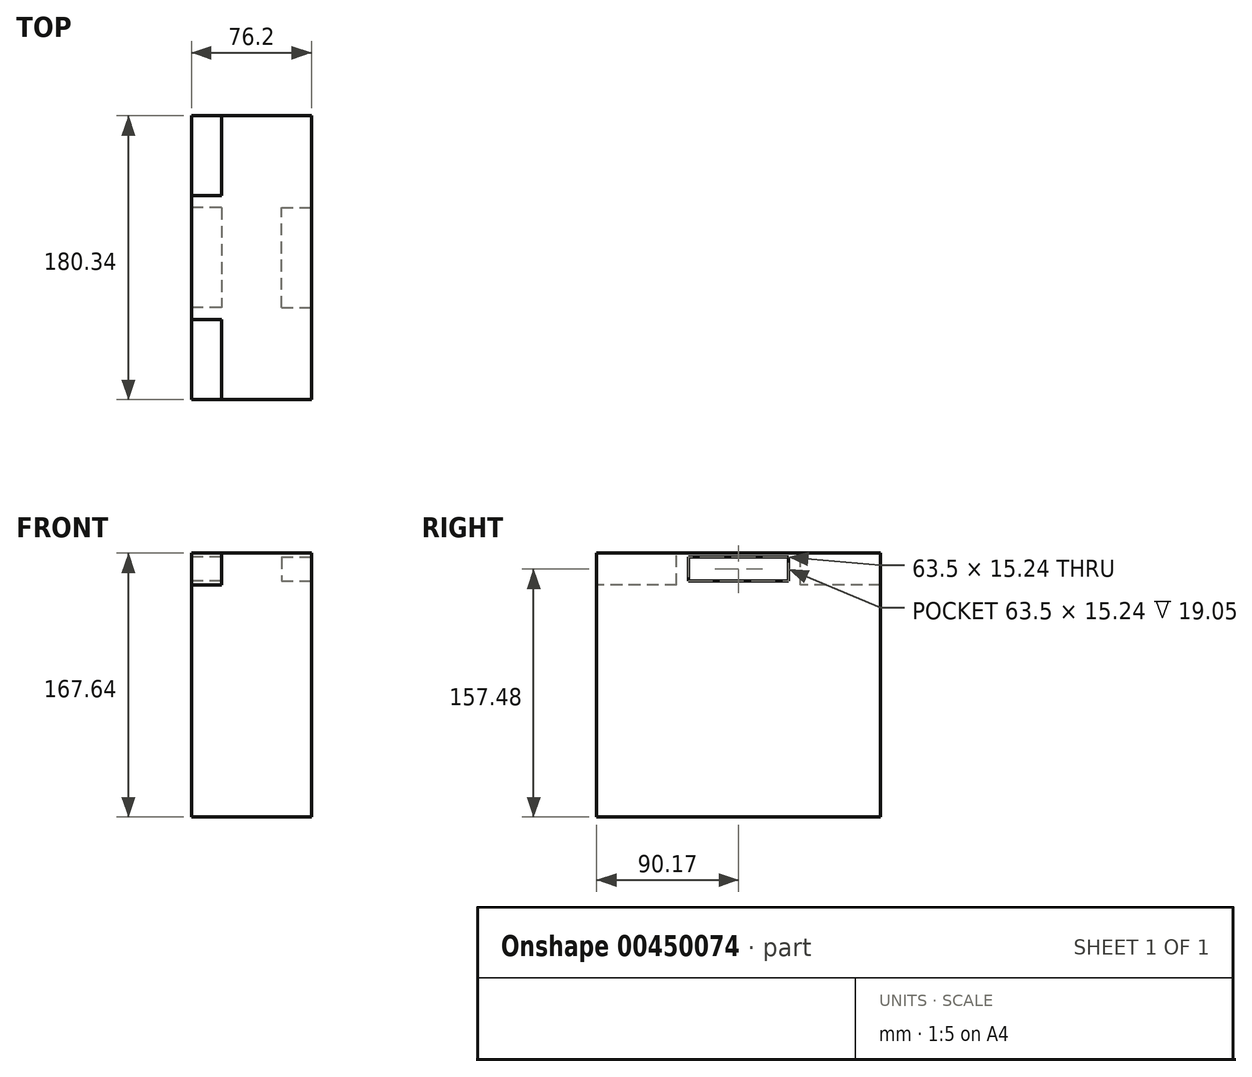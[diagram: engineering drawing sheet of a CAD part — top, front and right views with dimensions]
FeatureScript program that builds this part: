
annotation { "Feature Type Name" : "Feature", "Feature Type Description" : "" }
export const myFeature = defineFeature(function(context is Context, id is Id, definition is map)
    precondition{}
    {
        {
            var Q0;
            Q0=qCreatedBy(makeId("Top.planeOp"),FACE);
            var sketch = newSketch(context, id + "F0", { "sketchPlane" : qUnion([Q0])});
            skLineSegment(sketch, "E0.bottom", {"start": v(-38.1, 90.17) * mm, "end": v(38.1, 90.17) * mm});
            skLineSegment(sketch, "E0.top", {"start": v(-38.1, -90.17) * mm, "end": v(38.1, -90.17) * mm});
            skLineSegment(sketch, "E0.left", {"start": v(-38.1, 90.17) * mm, "end": v(-38.1, -90.17) * mm});
            skLineSegment(sketch, "E0.right", {"start": v(38.1, 90.17) * mm, "end": v(38.1, -90.17) * mm});
            skPoint(sketch, "E0.middle", {"position": v(0, 0) * mm});
            skSolve(sketch);
        }
        {
            var Q0;
            Q0=makeQuery(id+"F0.imprint","IMPRINT",FACE,{"disambiguationData":[TD([[makeQuery(id+"F0.imprint","IMPRINT",EDGE,{"derivedFrom":sQuery(id+"F0.wireOp",EDGE,"E0.bottom")}),-1.0]])]});
            extrude(context, id + "F1", {"entities" : qUnion([Q0]), "depth" : 167.64 * mm});
        }
        {
            var Q0;
            Q0=makeQuery(id+"F1.opExtrude","CAP_FACE",FACE,{"disambiguationData":[OSD([sQuery(id+"F0.wireOp",EDGE,"E0.bottom"),sQuery(id+"F0.wireOp",EDGE,"E0.top"),sQuery(id+"F0.wireOp",EDGE,"E0.left"),sQuery(id+"F0.wireOp",EDGE,"E0.right")])],"isStart":false});
            var sketch = newSketch(context, id + "F2", { "sketchPlane" : qUnion([Q0])});
            skLineSegment(sketch, "E1.bottom", {"start": v(-38.1, -90.17) * mm, "end": v(-19.05, -90.17) * mm});
            skLineSegment(sketch, "E1.top", {"start": v(-38.1, -39.37) * mm, "end": v(-19.05, -39.37) * mm});
            skLineSegment(sketch, "E1.left", {"start": v(-38.1, -90.17) * mm, "end": v(-38.1, -39.37) * mm});
            skLineSegment(sketch, "E1.right", {"start": v(-19.05, -90.17) * mm, "end": v(-19.05, -39.37) * mm});
            skLineSegment(sketch, "E2.bottom", {"start": v(-38.1, 90.17) * mm, "end": v(-19.05, 90.17) * mm});
            skLineSegment(sketch, "E2.top", {"start": v(-38.1, 39.37) * mm, "end": v(-19.05, 39.37) * mm});
            skLineSegment(sketch, "E2.left", {"start": v(-38.1, 90.17) * mm, "end": v(-38.1, 39.37) * mm});
            skLineSegment(sketch, "E2.right", {"start": v(-19.05, 90.17) * mm, "end": v(-19.05, 39.37) * mm});
            skSolve(sketch);
        }
        {
            var Q0;
            Q0=makeQuery(id+"F2.imprint","IMPRINT",FACE,{"disambiguationData":[TD([[makeQuery(id+"F2.imprint","IMPRINT",EDGE,{"derivedFrom":sQuery(id+"F2.wireOp",EDGE,"E1.bottom")}),1.0]])]});
            var Q1;
            Q1=makeQuery(id+"F2.imprint","IMPRINT",FACE,{"disambiguationData":[TD([[makeQuery(id+"F2.imprint","IMPRINT",EDGE,{"derivedFrom":sQuery(id+"F2.wireOp",EDGE,"E2.bottom")}),-1.0]])]});
            extrude(context, id + "F3", {"entities" : qUnion([Q0, Q1]), "operationType" : NewBodyOperationType.REMOVE, "oppositeDirection" : true, "depth" : 20.32 * mm});
        }
        {
            var Q0;
            Q0=makeQuery(id+"F1.opExtrude","SWEPT_FACE",FACE,{"disambiguationData":[OSD([sQuery(id+"F0.wireOp",EDGE,"E0.left")])]});
            var sketch = newSketch(context, id + "F4", { "sketchPlane" : qUnion([Q0])});
            skLineSegment(sketch, "E3.bottom", {"start": v(-31.75, 165.1) * mm, "end": v(31.75, 165.1) * mm});
            skLineSegment(sketch, "E3.top", {"start": v(-31.75, 149.86) * mm, "end": v(31.75, 149.86) * mm});
            skLineSegment(sketch, "E3.left", {"start": v(-31.75, 165.1) * mm, "end": v(-31.75, 149.86) * mm});
            skLineSegment(sketch, "E3.right", {"start": v(31.75, 165.1) * mm, "end": v(31.75, 149.86) * mm});
            skPoint(sketch, "E3.middle", {"position": v(0, 157.48) * mm});
            skSolve(sketch);
        }
        {
            var Q0;
            Q0=makeQuery(id+"F4.imprint","IMPRINT",FACE,{"disambiguationData":[TD([[makeQuery(id+"F4.imprint","IMPRINT",EDGE,{"derivedFrom":sQuery(id+"F4.wireOp",EDGE,"E3.bottom")}),-1.0]])]});
            extrude(context, id + "F5", {"entities" : qUnion([Q0]), "operationType" : NewBodyOperationType.REMOVE, "oppositeDirection" : true, "depth" : 19.05 * mm});
        }
        {
            var Q0;
            Q0=makeQuery(id+"F1.opExtrude","SWEPT_FACE",FACE,{"disambiguationData":[OSD([sQuery(id+"F0.wireOp",EDGE,"E0.right")])]});
            var sketch = newSketch(context, id + "F6", { "sketchPlane" : qUnion([Q0])});
            skLineSegment(sketch, "E4.bottom", {"start": v(-31.75, 165.1) * mm, "end": v(31.75, 165.1) * mm});
            skLineSegment(sketch, "E4.top", {"start": v(-31.75, 149.86) * mm, "end": v(31.75, 149.86) * mm});
            skLineSegment(sketch, "E4.left", {"start": v(-31.75, 165.1) * mm, "end": v(-31.75, 149.86) * mm});
            skLineSegment(sketch, "E4.right", {"start": v(31.75, 165.1) * mm, "end": v(31.75, 149.86) * mm});
            skPoint(sketch, "E4.middle", {"position": v(0, 157.48) * mm});
            skSolve(sketch);
        }
        {
            var Q0;
            Q0=makeQuery(id+"F6.imprint","IMPRINT",FACE,{"disambiguationData":[TD([[makeQuery(id+"F6.imprint","IMPRINT",EDGE,{"derivedFrom":sQuery(id+"F6.wireOp",EDGE,"E4.bottom")}),-1.0]])]});
            extrude(context, id + "F7", {"entities" : qUnion([Q0]), "operationType" : NewBodyOperationType.REMOVE, "oppositeDirection" : true, "depth" : 19.05 * mm});
        }
    });
